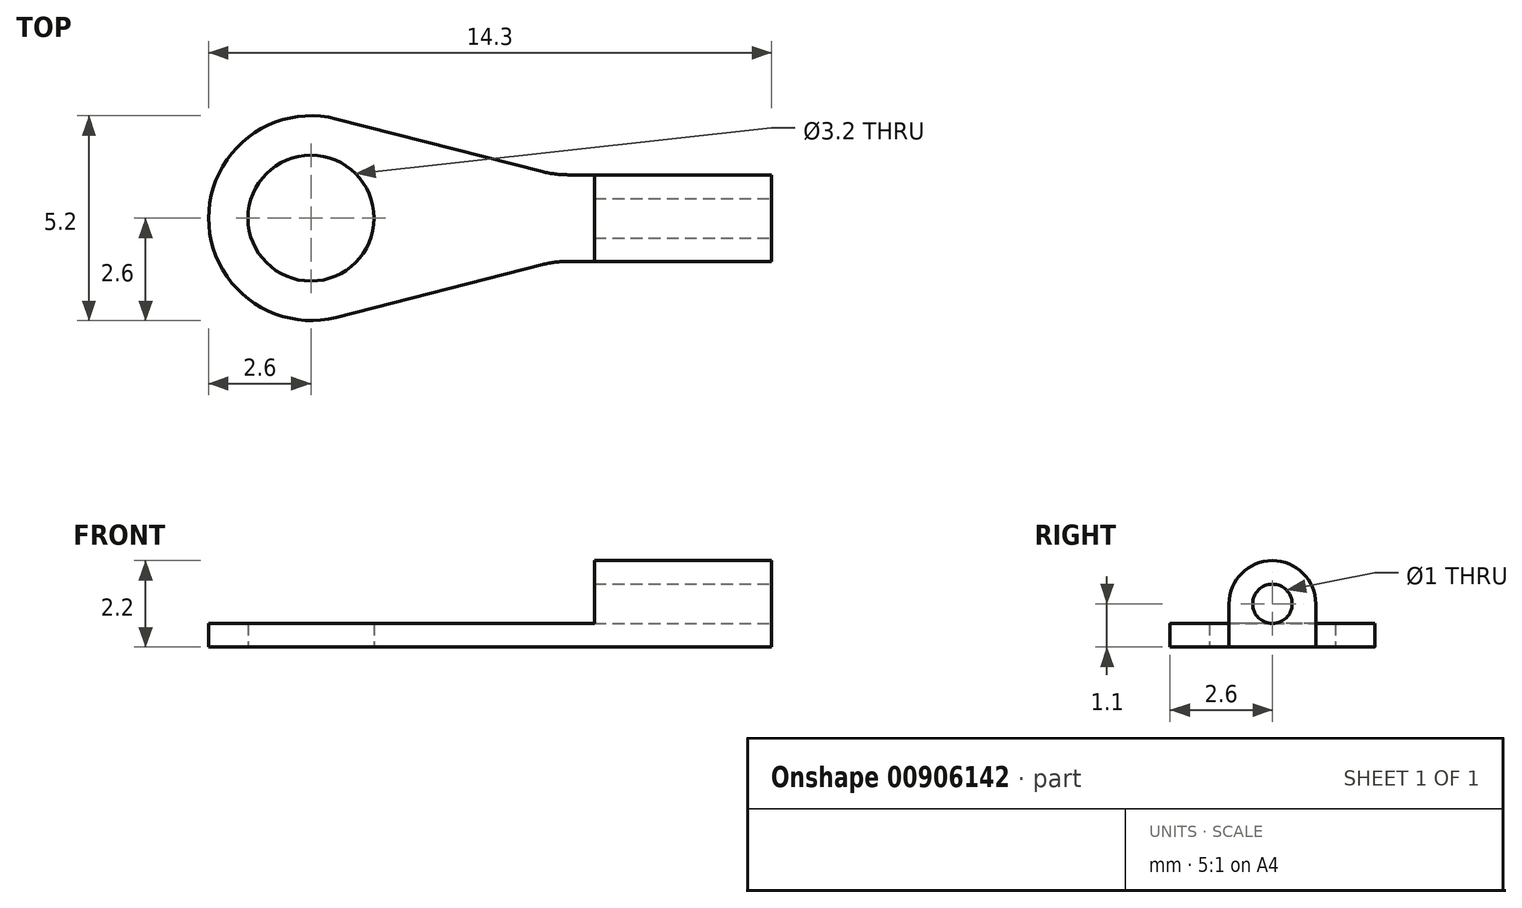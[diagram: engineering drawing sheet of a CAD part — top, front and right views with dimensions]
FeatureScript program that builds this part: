
annotation { "Feature Type Name" : "Feature", "Feature Type Description" : "" }
export const myFeature = defineFeature(function(context is Context, id is Id, definition is map)
    precondition{}
    {
        {
            var Q0;
            Q0=qCreatedBy(makeId("Top.planeOp"),FACE);
            var sketch = newSketch(context, id + "F0", { "sketchPlane" : qUnion([Q0])});
            skLineSegment(sketch, "E0.left", {"start": v(0, 2.6) * mm, "end": v(0, 2.6) * mm});
            skLineSegment(sketch, "E0.right", {"start": v(14.3, 1.5) * mm, "end": v(14.3, 3.7) * mm});
            skPoint(sketch, "E1.visualSharp", {"position": v(0, 5.2) * mm});
            skArc(sketch, "E1.filletArc", {"start": v(2.6, 5.2) * mm, "mid": v(0.76, 4.44) * mm, "end": v(0, 2.6) * mm});
            skPoint(sketch, "E2.visualSharp", {"position": v(0, 0) * mm});
            skArc(sketch, "E2.filletArc", {"start": v(0, 2.6) * mm, "mid": v(0.76, 0.76) * mm, "end": v(2.6, 0) * mm});
            skLineSegment(sketch, "E3.0", {"start": v(9.8, 1.5) * mm, "end": v(9.8, 3.7) * mm});
            skLineSegment(sketch, "E4.0", {"start": v(8.8, 1.48) * mm, "end": v(8.8, 3.72) * mm});
            skLineSegment(sketch, "E5.0", {"start": v(2.6, 0) * mm, "end": v(2.6, 5.2) * mm});
            skCircle(sketch, "E6", {"center": v(2.6, 2.6) * mm, "radius": 1.6 * mm});
            skArc(sketch, "E7", {"start": v(3.24, 5.12) * mm, "mid": v(0, 2.6) * mm, "end": v(3.24, 0.08) * mm});
            skLineSegment(sketch, "E8", {"start": v(14.3, 2.6) * mm, "end": v(8.8, 2.6) * mm});
            skLineSegment(sketch, "E9.0", {"start": v(14.3, 3.7) * mm, "end": v(9.13, 3.7) * mm});
            skLineSegment(sketch, "E10.0", {"start": v(14.3, 1.5) * mm, "end": v(9.13, 1.5) * mm});
            skLineSegment(sketch, "E11", {"start": v(8.48, 3.78) * mm, "end": v(3.24, 5.12) * mm});
            skLineSegment(sketch, "E12", {"start": v(8.48, 1.42) * mm, "end": v(3.24, 0.08) * mm});
            skPoint(sketch, "E13.visualSharp", {"position": v(8.8, 3.7) * mm});
            skArc(sketch, "E13.filletArc", {"start": v(8.48, 3.78) * mm, "mid": v(8.8, 3.72) * mm, "end": v(9.13, 3.7) * mm});
            skPoint(sketch, "E14.visualSharp", {"position": v(8.8, 1.5) * mm});
            skArc(sketch, "E14.filletArc", {"start": v(9.13, 1.5) * mm, "mid": v(8.8, 1.48) * mm, "end": v(8.48, 1.42) * mm});
            skPoint(sketch, "E15.orphan", {"position": v(8.8, 5.2) * mm});
            skPoint(sketch, "E16.orphan", {"position": v(14.3, 5.2) * mm});
            skPoint(sketch, "E17.orphan", {"position": v(14.3, 0) * mm});
            skPoint(sketch, "E0.bottom.end.orphan", {"position": v(8.8, 0) * mm});
            skSolve(sketch);
        }
        {
            var Q0;
            Q0 = qSketchRegion(id + "F0", true);
            extrude(context, id + "F1", {"entities" : qUnion([Q0]), "depth" : 0.6 * mm, "offsetDistance" : 25 * mm});
        }
        {
            var Q0;
            Q0=makeQuery(id+"F1.opExtrude","CAP_FACE",FACE,{"disambiguationData":[OSD([sQuery(id+"F0.wireOp",EDGE,"E0.right"),sQuery(id+"F0.wireOp",EDGE,"E6"),sQuery(id+"F0.wireOp",EDGE,"E7"),sQuery(id+"F0.wireOp",EDGE,"E9.0"),sQuery(id+"F0.wireOp",EDGE,"E10.0"),sQuery(id+"F0.wireOp",EDGE,"E11"),sQuery(id+"F0.wireOp",EDGE,"E12"),sQuery(id+"F0.wireOp",EDGE,"E13.filletArc"),sQuery(id+"F0.wireOp",EDGE,"E14.filletArc")])],"isStart":false});
            var sketch = newSketch(context, id + "F2", { "sketchPlane" : qUnion([Q0])});
            skLineSegment(sketch, "E18.bottom", {"start": v(14.3, 3.7) * mm, "end": v(9.8, 3.7) * mm});
            skLineSegment(sketch, "E18.top", {"start": v(14.3, 1.5) * mm, "end": v(9.8, 1.5) * mm});
            skLineSegment(sketch, "E18.left", {"start": v(14.3, 3.7) * mm, "end": v(14.3, 1.5) * mm});
            skLineSegment(sketch, "E18.right", {"start": v(9.8, 3.7) * mm, "end": v(9.8, 1.5) * mm});
            skSolve(sketch);
        }
        {
            var Q0;
            Q0 = qSketchRegion(id + "F2", true);
            extrude(context, id + "F3", {"entities" : qUnion([Q0]), "operationType" : NewBodyOperationType.ADD, "depth" : 1.6 * mm, "offsetDistance" : 25 * mm});
        }
        {
            var Q0;
            Q0=makeQuery(id+"F3.opExtrude","CAP_EDGE",EDGE,{"disambiguationData":[OSD([sQuery(id+"F2.wireOp",EDGE,"E18.top")])],"isStart":false});
            var Q1;
            Q1=makeQuery(id+"F3.opExtrude","CAP_EDGE",EDGE,{"disambiguationData":[OSD([sQuery(id+"F2.wireOp",EDGE,"E18.bottom")])],"isStart":false});
            fillet(context, id + "F4", {"entities" : qUnion([Q0, Q1]), "radius" : 1.1 * mm, "tangentPropagation" : true, "allowEdgeOverflow" : false});
        }
        {
            var Q0;
            Q0=makeQuery(id+"F3.boolean.opBoolean","MERGE",FACE,{"derivedFrom":[makeQuery(id+"F1.opExtrude","SWEPT_FACE",FACE,{"disambiguationData":[OSD([sQuery(id+"F0.wireOp",EDGE,"E0.right")])]}),makeQuery(id+"F3.opExtrude","SWEPT_FACE",FACE,{"disambiguationData":[OSD([sQuery(id+"F2.wireOp",EDGE,"E18.left")])]})]});
            var sketch = newSketch(context, id + "F5", { "sketchPlane" : qUnion([Q0])});
            skCircle(sketch, "E19", {"center": v(2.6, 1.1) * mm, "radius": 0.5 * mm});
            skSolve(sketch);
        }
        {
            var Q0;
            Q0=makeQuery(id+"F5.imprint","IMPRINT",FACE,{"disambiguationData":[TD([[makeQuery(id+"F5.imprint","IMPRINT",EDGE,{"derivedFrom":sQuery(id+"F5.wireOp",EDGE,"E19")}),1.0]])]});
            var Q1;
            Q1=sQuery(id+"F5.wireOp",EDGE,"E19");
            extrude(context, id + "F6", {"entities" : qUnion([Q0]), "operationType" : NewBodyOperationType.REMOVE, "surfaceEntities" : qUnion([Q1]), "oppositeDirection" : true, "depth" : 25 * mm, "offsetDistance" : 25 * mm});
        }
    });
